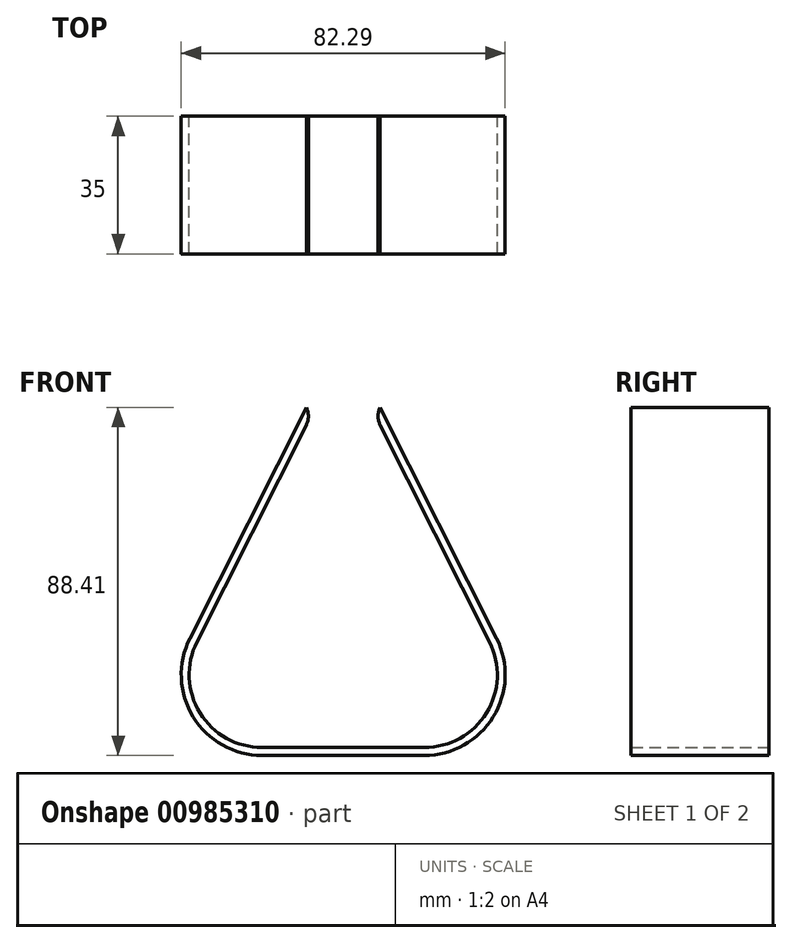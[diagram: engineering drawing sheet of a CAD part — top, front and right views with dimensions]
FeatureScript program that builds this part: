
annotation { "Feature Type Name" : "Feature", "Feature Type Description" : "" }
export const myFeature = defineFeature(function(context is Context, id is Id, definition is map)
    precondition{}
    {
        {
            var Q0;
            Q0=qCreatedBy(makeId("Front.planeOp"),FACE);
            var sketch = newSketch(context, id + "F0", { "sketchPlane" : qUnion([Q0])});
            skPoint(sketch, "E0.visualSharp", {"position": v(-69.9, -1.36) * mm});
            skPoint(sketch, "E1.visualSharp", {"position": v(20.1, -1.36) * mm});
            skLineSegment(sketch, "E2.0", {"start": v(-17.32, 80.65) * mm, "end": v(12.26, 21.96) * mm});
            skLineSegment(sketch, "E2.1", {"start": v(-32.5, 80.65) * mm, "end": v(-62.07, 21.96) * mm});
            skArc(sketch, "E2.2", {"start": v(-62.07, 21.96) * mm, "mid": v(-61.3, 3.94) * mm, "end": v(-45.55, -4.86) * mm});
            skLineSegment(sketch, "E2.3", {"start": v(-45.55, -4.86) * mm, "end": v(-4.26, -4.86) * mm});
            skArc(sketch, "E2.4", {"start": v(-4.26, -4.86) * mm, "mid": v(11.5, 3.94) * mm, "end": v(12.26, 21.96) * mm});
            skLineSegment(sketch, "E3.0", {"start": v(-15.53, 81.55) * mm, "end": v(14.05, 22.86) * mm});
            skLineSegment(sketch, "E3.1", {"start": v(-34.28, 81.55) * mm, "end": v(-63.86, 22.86) * mm});
            skArc(sketch, "E3.2", {"start": v(-63.86, 22.86) * mm, "mid": v(-63, 2.89) * mm, "end": v(-45.55, -6.86) * mm});
            skLineSegment(sketch, "E3.3", {"start": v(-45.55, -6.86) * mm, "end": v(-4.26, -6.86) * mm});
            skArc(sketch, "E3.4", {"start": v(-4.26, -6.86) * mm, "mid": v(13.2, 2.89) * mm, "end": v(14.05, 22.86) * mm});
            skLineSegment(sketch, "E4", {"start": v(-34.28, 81.55) * mm, "end": v(-32.5, 80.65) * mm});
            skLineSegment(sketch, "E5", {"start": v(-17.32, 80.65) * mm, "end": v(-15.53, 81.55) * mm});
            skSolve(sketch);
        }
        {
            var Q0;
            Q0 = qSketchRegion(id + "F0", true);
            extrude(context, id + "F1", {"entities" : qUnion([Q0]), "depth" : 35 * mm, "offsetDistance" : 25 * mm});
        }
        {
            var Q0;
            Q0=makeQuery(id+"F1.opExtrude","SWEPT_EDGE",EDGE,{"disambiguationData":[OSD([sQuery(id+"F0.wireOp",EDGE,"E2.1"),sQuery(id+"F0.wireOp",EDGE,"E4")])]});
            var Q1;
            Q1=makeQuery(id+"F1.opExtrude","SWEPT_EDGE",EDGE,{"disambiguationData":[OSD([sQuery(id+"F0.wireOp",EDGE,"E2.0"),sQuery(id+"F0.wireOp",EDGE,"E5")])]});
            fillet(context, id + "F2", {"entities" : qUnion([Q0, Q1]), "radius" : 5 * mm, "tangentPropagation" : true, "allowEdgeOverflow" : false});
        }
    });
